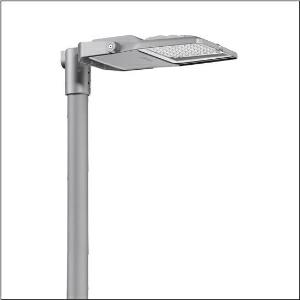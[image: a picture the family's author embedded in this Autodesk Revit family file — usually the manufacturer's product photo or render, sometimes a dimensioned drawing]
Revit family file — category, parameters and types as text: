
# Revit family: floodlight_fl_21_iq_mini___pl43_5xa7771b4a3a_ae81
name_source: partatom
category: Lighting Fixtures
units: mm (PartAtom-declared; Revit-internal decimal feet)

## family parameters
Cut with Voids When Loaded = No
Host = Face
Light Source = No
Part Type = Normal
Room Calculation Point = No
Round Connector Dimension = Use Diameter
Shared = No

## types (1)
- --- (1 x LED, 6660 lm, 45.5 W, 4000K)
    Apparent Load = 46 VA
    CIE Flux Codes = 27 78 99 100 100
    Color Rendering = 70
    Color Temperature = 4000K
    Default Elevation = 1800 mm
    Description = Floodlight FL 21 iQ mini, floodlight, primary light control with lens, of PMMA, primary optical cover: protective disc, of toughened safety glass, transparent, light distribution: PL43, light emission: direct distribution, installation type: surface-mounted, LED, High Power LED, rated luminous flux: 6.660lm, luminous efficacy: 146lm/W, light colour: 740, colour temperature: 4000K, control: Auto-Match, Temp-Guard, Lumen-Switch, Night-Set, Smart-Wire, Light-Fading, Desk-Remote (wireless, voltage-free reading and setting of iQ features in the workshop via application-optimized NFC function/RFID function), optimised constant luminous flux control (CLO 2.0), with terminal, 6-pole, mains connection: 220..240V, AC, 50/60Hz, start of lifetime: 46W, end of service life: 48W, reduction: 22W, luminaire housing, of diecast aluminium, powder-coated, Siteco® metallic grey (DB 702S), corrosivity category C5 mid according to DIN EN ISO 12944, sealing non-destructively replaceable, please order mast flange separately, mast bracket, of steel, galvanised, powder-coated, Siteco® metallic grey (DB 702S), protection rating (complete): IP66, insulation class (complete): insulation class II (safety insulation), certification: CE, ENEC, VDE, protection symbol: D, impact resistance: IK08, permissible operating ambient temperature: -40..+40°C, permissible operating ambient temperature for outdoor applications: -40..+50°C, standard: DIN EN 12944, LABS conformity tested according to VDMA 24364:2018-05, packaging unit: 1 piece

Light Distribution: PL43
    Height = 70 mm
    Lamp = 1 x LED
    Lamp Light Flux = 6660 lm
    Lamp Power = 45.5 W
    Lamp count = 1
    Length = 485 mm
    Luminous efficacy = 146 lm/W
    Manufacturer = Siteco
    ModVariant = No
    Model = 5XA7771B4A3A
    Number of Poles = 1
    OnlyDefault = Yes
    Power Factor = 1
    Product Name = Floodlight FL 21 iQ mini | PL43
    Product group = floodlight | pylon annexe
    ProductGroupID = 6200
    Protection Class = Protection class II
    Protection Degree = IP 66
    RLX_Detail_Level = 1
    RLX_Emergency_Light_Flux = 0 lm
    RLX_Emergency_Type = 0
    RLX_Emergency_Type_DB = No
    RlxData = <blob elided: 101129 chars, md5=5a87b4a2>
    Socket = socket
    Standby Power = 0 W
    System Light Flux = 6660 lm
    System Power = 46 W
    Type Comments = factory setting: luminous flux: 100 % | dim-lin: 254 | 463 mA
    Type Image = l_1007125.jpg
    URL = http://relux.com
    VarID = @adj_095197
    Voltage = 0 V
    Weight = 0.00 kg
    Width = 337 mm

## geometry (parser evidence)
native form markers: Blend x4, Sweep x13
no freeform markers — native parametric forms only
